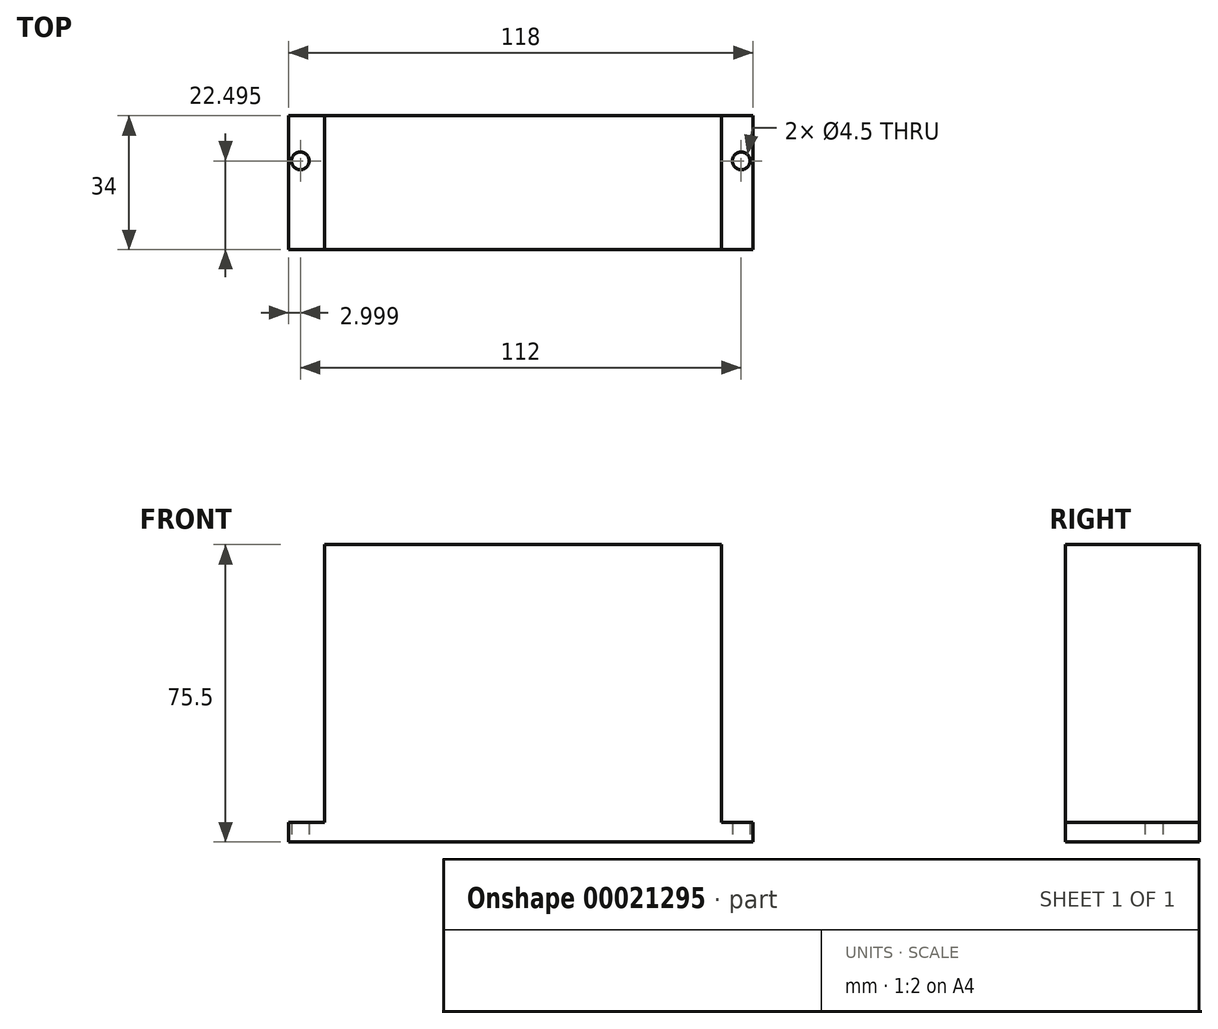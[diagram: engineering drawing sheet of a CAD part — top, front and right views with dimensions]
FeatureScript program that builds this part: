
annotation { "Feature Type Name" : "Feature", "Feature Type Description" : "" }
export const myFeature = defineFeature(function(context is Context, id is Id, definition is map)
    precondition{}
    {
        {
            var Q0;
            Q0=qCreatedBy(makeId("Top.planeOp"),FACE);
            var sketch = newSketch(context, id + "F0", { "sketchPlane" : qUnion([Q0])});
            skLineSegment(sketch, "E0.bottom", {"start": v(-55.37, 5.26) * mm, "end": v(62.63, 5.26) * mm});
            skLineSegment(sketch, "E0.top", {"start": v(-55.37, -28.74) * mm, "end": v(62.63, -28.74) * mm});
            skLineSegment(sketch, "E0.left", {"start": v(-55.37, 5.26) * mm, "end": v(-55.37, -28.74) * mm});
            skLineSegment(sketch, "E0.right", {"start": v(62.63, 5.26) * mm, "end": v(62.63, -28.74) * mm});
            skLineSegment(sketch, "E1", {"start": v(-55.37, -6.24) * mm, "end": v(62.63, -6.24) * mm, "construction": true});
            skCircle(sketch, "E2", {"center": v(-52.37, -6.24) * mm, "radius": 2.25 * mm});
            skCircle(sketch, "E3", {"center": v(59.63, -6.24) * mm, "radius": 2.25 * mm});
            skLineSegment(sketch, "E4", {"start": v(3.63, -28.74) * mm, "end": v(3.63, 5.26) * mm, "construction": true});
            skSolve(sketch);
        }
        {
            var Q0;
            Q0=makeQuery(id+"F0.imprint","IMPRINT",FACE,{"disambiguationData":[TD([[makeQuery(id+"F0.imprint","IMPRINT",EDGE,{"derivedFrom":sQuery(id+"F0.wireOp",EDGE,"E0.bottom")}),-1.0]])]});
            extrude(context, id + "F1", {"entities" : qUnion([Q0]), "depth" : 75.5 * mm});
        }
        {
            var Q0;
            Q0=makeQuery(id+"F1.opExtrude","CAP_FACE",FACE,{"disambiguationData":[OSD([sQuery(id+"F0.wireOp",EDGE,"E0.bottom"),sQuery(id+"F0.wireOp",EDGE,"E0.top"),sQuery(id+"F0.wireOp",EDGE,"E0.left"),sQuery(id+"F0.wireOp",EDGE,"E0.right"),sQuery(id+"F0.wireOp",EDGE,"E2"),sQuery(id+"F0.wireOp",EDGE,"E3")])],"isStart":false});
            var sketch = newSketch(context, id + "F2", { "sketchPlane" : qUnion([Q0])});
            skLineSegment(sketch, "E5.bottom", {"start": v(-55.37, 5.26) * mm, "end": v(-46.28, 5.26) * mm});
            skLineSegment(sketch, "E5.top", {"start": v(-55.37, -28.74) * mm, "end": v(-46.28, -28.74) * mm});
            skLineSegment(sketch, "E5.left", {"start": v(-55.37, 5.26) * mm, "end": v(-55.37, -28.74) * mm});
            skLineSegment(sketch, "E5.right", {"start": v(-46.28, 5.26) * mm, "end": v(-46.28, -28.74) * mm});
            skLineSegment(sketch, "E6.bottom", {"start": v(62.63, -28.74) * mm, "end": v(54.63, -28.74) * mm});
            skLineSegment(sketch, "E6.top", {"start": v(62.63, 5.26) * mm, "end": v(54.63, 5.26) * mm});
            skLineSegment(sketch, "E6.left", {"start": v(62.63, -28.74) * mm, "end": v(62.63, 5.26) * mm});
            skLineSegment(sketch, "E6.right", {"start": v(54.63, -28.74) * mm, "end": v(54.63, 5.26) * mm});
            skSolve(sketch);
        }
        {
            var Q0;
            Q0 = qSketchRegion(id + "F2", true);
            extrude(context, id + "F3", {"entities" : qUnion([Q0]), "operationType" : NewBodyOperationType.REMOVE, "oppositeDirection" : true, "depth" : 70.58 * mm});
        }
    });
